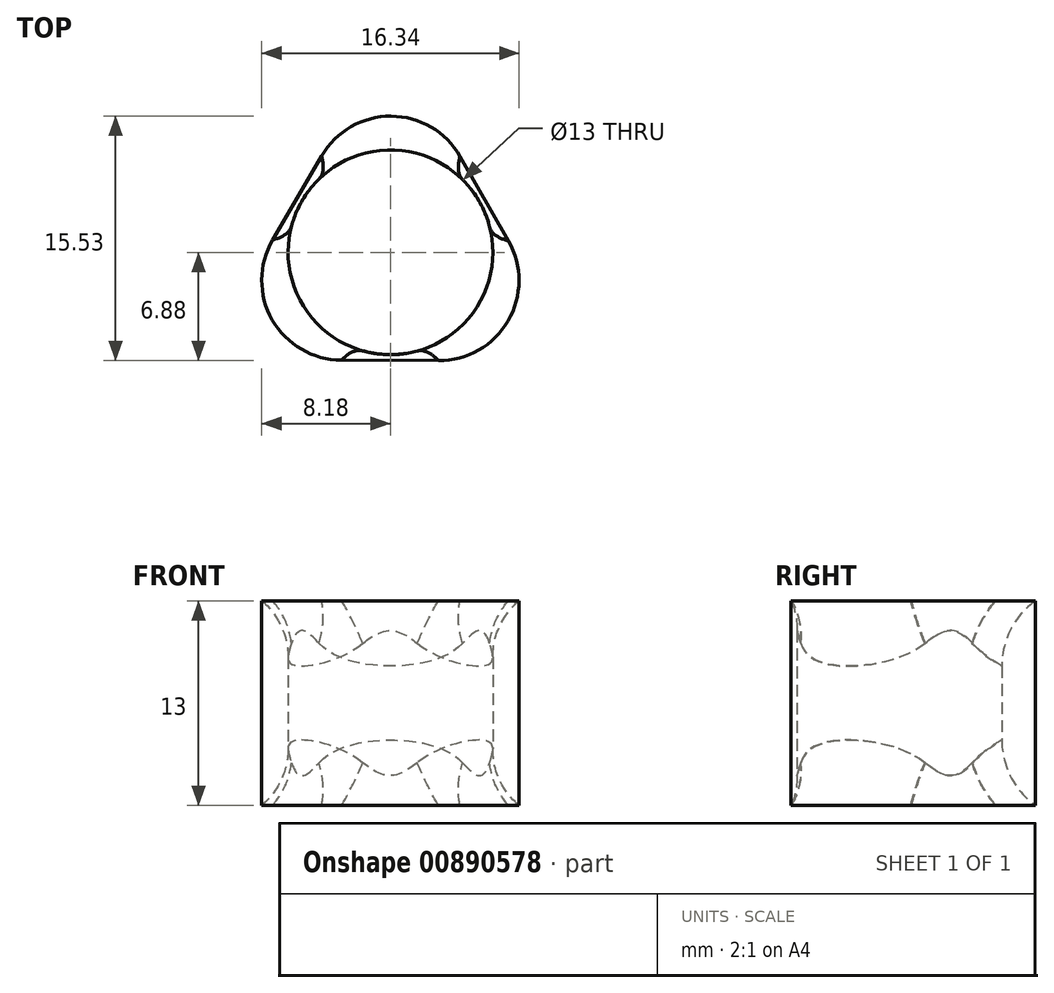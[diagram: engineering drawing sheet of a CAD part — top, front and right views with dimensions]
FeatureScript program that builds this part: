
annotation { "Feature Type Name" : "Feature", "Feature Type Description" : "" }
export const myFeature = defineFeature(function(context is Context, id is Id, definition is map)
    precondition{}
    {
        {
            var Q0;
            Q0=qCreatedBy(makeId("Top.planeOp"),FACE);
            var sketch = newSketch(context, id + "F0", { "sketchPlane" : qUnion([Q0])});
            skCircle(sketch, "E0.cCircle", {"center": v(0, 0) * mm, "radius": 6.86 * mm, "construction": true});
            skLineSegment(sketch, "E0.0", {"start": v(-11.92, -6.81) * mm, "end": v(0.06, 13.73) * mm});
            skLineSegment(sketch, "E0.1", {"start": v(0.06, 13.73) * mm, "end": v(11.86, -6.91) * mm});
            skLineSegment(sketch, "E0.2", {"start": v(11.86, -6.91) * mm, "end": v(-11.92, -6.81) * mm});
            skPoint(sketch, "E0.0.midPoint", {"position": v(-5.93, 3.46) * mm});
            skCircle(sketch, "E1", {"center": v(0, 0) * mm, "radius": 6.5 * mm});
            skSolve(sketch);
        }
        {
            var Q0;
            Q0 = qSketchRegion(id + "F0", true);
            extrude(context, id + "F1", {"entities" : qUnion([Q0]), "depth" : 13 * mm, "offsetDistance" : 25.4 * mm});
        }
        {
            var Q0;
            Q0=makeQuery(id+"F1.opExtrude","SWEPT_EDGE",EDGE,{"disambiguationData":[OSD([sQuery(id+"F0.wireOp",EDGE,"E0.0"),sQuery(id+"F0.wireOp",EDGE,"E0.1")])]});
            fillet(context, id + "F2", {"entities" : qUnion([Q0]), "radius" : 5.08 * mm, "tangentPropagation" : true, "allowEdgeOverflow" : false});
        }
        {
            var Q0;
            Q0=makeQuery(id+"F1.opExtrude","SWEPT_EDGE",EDGE,{"disambiguationData":[OSD([sQuery(id+"F0.wireOp",EDGE,"E0.1"),sQuery(id+"F0.wireOp",EDGE,"E0.2")])]});
            fillet(context, id + "F3", {"entities" : qUnion([Q0]), "radius" : 5.08 * mm, "tangentPropagation" : true, "allowEdgeOverflow" : false});
        }
        {
            var Q0;
            Q0=makeQuery(id+"F1.opExtrude","SWEPT_EDGE",EDGE,{"disambiguationData":[OSD([sQuery(id+"F0.wireOp",EDGE,"E0.0"),sQuery(id+"F0.wireOp",EDGE,"E0.2")])]});
            fillet(context, id + "F4", {"entities" : qUnion([Q0]), "radius" : 5.08 * mm, "tangentPropagation" : true, "allowEdgeOverflow" : false});
        }
        {
            var Q0;
            Q0=makeQuery(id+"F1.opExtrude","CAP_EDGE",EDGE,{"disambiguationData":[OSD([sQuery(id+"F0.wireOp",EDGE,"E1")])],"isStart":true});
            fillet(context, id + "F5", {"entities" : qUnion([Q0]), "radius" : 5.08 * mm, "tangentPropagation" : true, "allowEdgeOverflow" : false});
        }
        {
            var Q0;
            Q0=makeQuery(id+"F1.opExtrude","CAP_EDGE",EDGE,{"disambiguationData":[OSD([sQuery(id+"F0.wireOp",EDGE,"E1")])],"isStart":false});
            fillet(context, id + "F6", {"entities" : qUnion([Q0]), "radius" : 5.08 * mm, "tangentPropagation" : true, "allowEdgeOverflow" : false});
        }
    });
